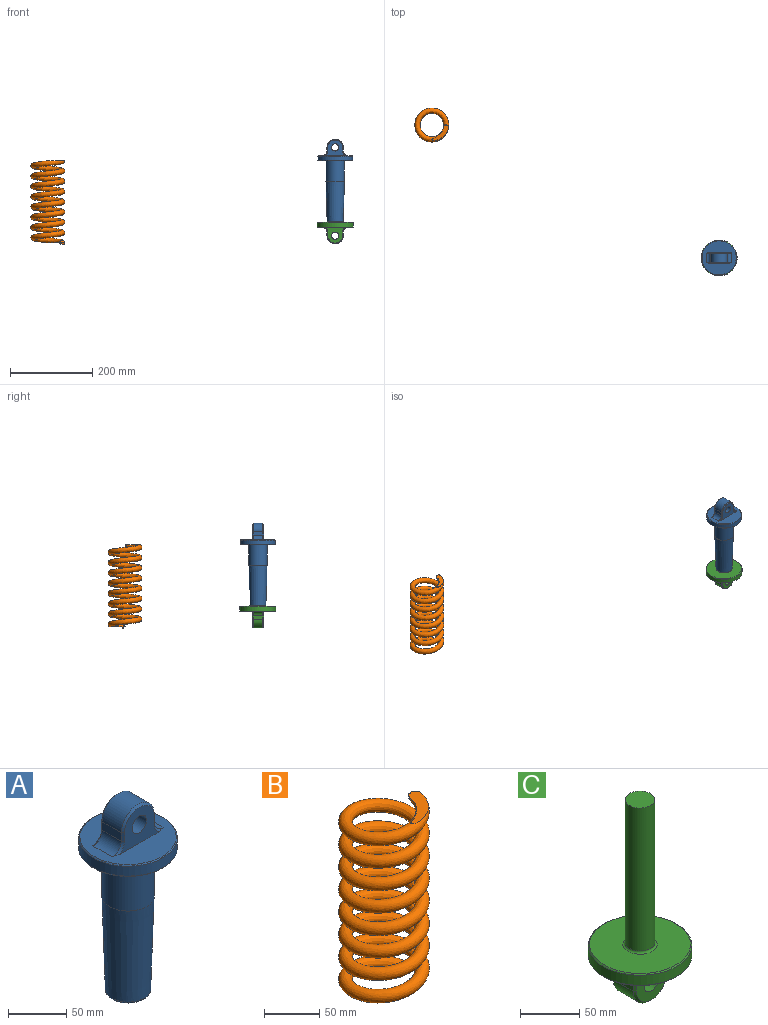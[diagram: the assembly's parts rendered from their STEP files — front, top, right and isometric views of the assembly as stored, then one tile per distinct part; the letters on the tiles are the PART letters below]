
ASSEMBLY  parts=3 mates=2
PART A: 30 faces, bbox 85x85x202.5 mm
  f0: plane 83x83mm, normal (0,0,1), area 3741.9mm2, adj f7,f9,f11,f14,f15,f16,f20,f21
  f1: cylinder r=13mm len=148mm, axis (0,0,1), area 12088.8mm2, adj f6,f29
  f2: cylinder r=22.5mm len=50mm, axis (0,0,1), area 7068.6mm2, adj f4,f27
  f3: plane 35.12x35.12mm, normal (0,0,-1), area 261.8mm2, adj f28,f29
  f4: plane 83x83mm, normal (0,0,-1), area 3820.2mm2, adj f2,f12
  f5: cylinder r=42.5mm len=85mm, axis (0,0,-1), area 2803.9mm2, adj f11,f12
  f6: plane 26x26mm, normal (0,0,-1), area 530.9mm2, adj f1
  f7: plane 48.14x38mm, normal (0,1,0), area 1027.7mm2, adj f0,f16,f17,f18,f19,f20,f26
  f8: plane 23.5x9mm, normal (-1,0,0), area 211.5mm2, adj f13,f14,f19,f22
  f9: plane 48.14x38mm, normal (0,-1,0), area 1027.7mm2, adj f0,f21,f22,f23,f24,f25,f26
  f10: plane 23.5x9mm, normal (1,0,0), area 211.5mm2, adj f13,f15,f17,f24
  f11: cone r=41.5mm half-angle=45deg, axis (0,0,-1), area 373.2mm2, adj f0,f5
  f12: cone r=42.5mm half-angle=45deg, axis (0,0,1), area 373.2mm2, adj f4,f5
  f13: cylinder r=20mm len=40mm, axis (0,-1,0), area 1476.5mm2, adj f8,f10,f18,f23
  f14: cylinder r=11mm len=23.5mm, axis (0,-1,0), area 406.1mm2, adj f0,f8,f20,f21
  f15: cylinder r=11mm len=23.5mm, axis (0,1,0), area 406.1mm2, adj f0,f10,f16,f25
  f16: cone r=13mm half-angle=45deg, axis (0,1,0), area 40mm2, adj f0,f7,f15,f17
  f17: plane 9x2mm, normal (0.71,0.71,0), area 25.5mm2, adj f7,f10,f16,f18
  f18: cone r=18mm half-angle=45deg, axis (0,-1,0), area 168.8mm2, adj f7,f13,f17,f19
  f19: plane 9x2mm, normal (-0.71,0.71,0), area 25.5mm2, adj f7,f8,f18,f20
  f20: cone r=13mm half-angle=45deg, axis (0,1,0), area 40mm2, adj f0,f7,f14,f19
  f21: cone r=13mm half-angle=45deg, axis (0,-1,0), area 40mm2, adj f0,f9,f14,f22
  f22: plane 9x2mm, normal (-0.71,-0.71,0), area 25.5mm2, adj f8,f9,f21,f23
  f23: cone r=18mm half-angle=45deg, axis (0,1,0), area 168.8mm2, adj f9,f13,f22,f24
  f24: plane 9x2mm, normal (0.71,-0.71,0), area 25.5mm2, adj f9,f10,f23,f25
  f25: cone r=13mm half-angle=45deg, axis (0,-1,0), area 40mm2, adj f0,f9,f15,f24
  f26: cylinder r=8.75mm len=27.5mm, axis (0,-1,0), area 1511.9mm2, adj f7,f9
  f27: cone r=22.5mm half-angle=1.7deg, axis (0,0,1), area 12962.5mm2, adj f2,f28
  f28: torus R=17.56mm, axis (0,0,1), area 364.4mm2, adj f3,f27
  f29: torus R=15mm, axis (0,0,1), area 271mm2, adj f1,f3
PART B: 8 faces, bbox 84.5x84x213.2 mm
  f0: plane 2.53x1.78mm, normal (0,1,0), area 3.8mm2, adj f1,f2
  f1: plane 40.88x37.32mm, normal (0,0,1), area 528.8mm2, adj f0,f2,f3
  f2: bspline ~13.26x10.13mm, area 110.7mm2, adj f0,f1,f3
  f3: bspline ~211.46x82.25mm, area 67407.9mm2, adj f1,f2,f4,f6
  f4: plane 42.61x39.04mm, normal (0,0,-1), area 529mm2, adj f3,f5,f6
  f5: plane 2.53x1.78mm, normal (0,-1,0), area 3.8mm2, adj f4,f6
  f6: bspline ~13.26x10.13mm, area 119.4mm2, adj f3,f4,f5
  f7: bspline ~13.26x12.27mm, area 0mm2
PART C: 26 faces, bbox 87.5x87.5x202.5 mm
  f0: cylinder r=43.75mm len=87.5mm, axis (0,0,1), area 2886.3mm2, adj f9,f10
  f1: plane 85.5x85.5mm, normal (0,0,-1), area 4072.8mm2, adj f3,f5,f9,f12,f13,f14,f18,f19
  f2: plane 85.5x85.5mm, normal (0,0,1), area 5080.9mm2, adj f10,f25
  f3: plane 48.14x38mm, normal (0,1,0), area 1027.7mm2, adj f1,f14,f15,f16,f17,f18,f24
  f4: plane 23.5x9mm, normal (1,0,0), area 211.5mm2, adj f11,f12,f17,f20
  f5: plane 48.14x38mm, normal (0,-1,0), area 1027.7mm2, adj f1,f19,f20,f21,f22,f23,f24
  f6: plane 23.5x9mm, normal (-1,0,0), area 211.5mm2, adj f11,f13,f15,f22
  f7: cylinder r=12.5mm len=148mm, axis (0,0,-1), area 11623.9mm2, adj f8,f25
  f8: plane 25x25mm, normal (0,0,1), area 490.9mm2, adj f7
  f9: cone r=43.75mm half-angle=45deg, axis (0,0,1), area 384.3mm2, adj f0,f1
  f10: cone r=42.75mm half-angle=45deg, axis (0,0,-1), area 384.3mm2, adj f0,f2
  f11: cylinder r=20mm len=40mm, axis (0,-1,0), area 1476.5mm2, adj f4,f6,f16,f21
  f12: cylinder r=11mm len=23.5mm, axis (0,1,0), area 406.1mm2, adj f1,f4,f18,f19
  f13: cylinder r=11mm len=23.5mm, axis (0,-1,0), area 406.1mm2, adj f1,f6,f14,f23
  f14: cone r=13mm half-angle=45deg, axis (0,1,0), area 40mm2, adj f1,f3,f13,f15
  f15: plane 9x2mm, normal (-0.71,0.71,0), area 25.5mm2, adj f3,f6,f14,f16
  f16: cone r=18mm half-angle=45deg, axis (0,-1,0), area 168.8mm2, adj f3,f11,f15,f17
  f17: plane 9x2mm, normal (0.71,0.71,0), area 25.5mm2, adj f3,f4,f16,f18
  f18: cone r=13mm half-angle=45deg, axis (0,1,0), area 40mm2, adj f1,f3,f12,f17
  f19: cone r=13mm half-angle=45deg, axis (0,-1,0), area 40mm2, adj f1,f5,f12,f20
  f20: plane 9x2mm, normal (0.71,-0.71,0), area 25.5mm2, adj f4,f5,f19,f21
  f21: cone r=18mm half-angle=45deg, axis (0,1,0), area 168.8mm2, adj f5,f11,f20,f22
  f22: plane 9x2mm, normal (-0.71,-0.71,0), area 25.5mm2, adj f5,f6,f21,f23
  f23: cone r=13mm half-angle=45deg, axis (0,-1,0), area 40mm2, adj f1,f5,f13,f22
  f24: cylinder r=8.75mm len=27.5mm, axis (0,-1,0), area 1511.9mm2, adj f3,f5
  f25: torus R=14.5mm, axis (0,0,1), area 261.1mm2, adj f2,f7
PLACE A t=(-244.67,-16.45,-9.63)mm fixed
PLACE B t=(-944.57,307.24,-9.63)mm
PLACE C t=(-244.67,-16.45,40.37)mm
MATE parallel A.f1 <-> C.f7  axis (0,0,-1) through (-244.67,-16.45,190.37)mm
MATE planar B.f1 <-> A.f5  axis (0,0,1) through (-944.57,307.24,190.37)mm
